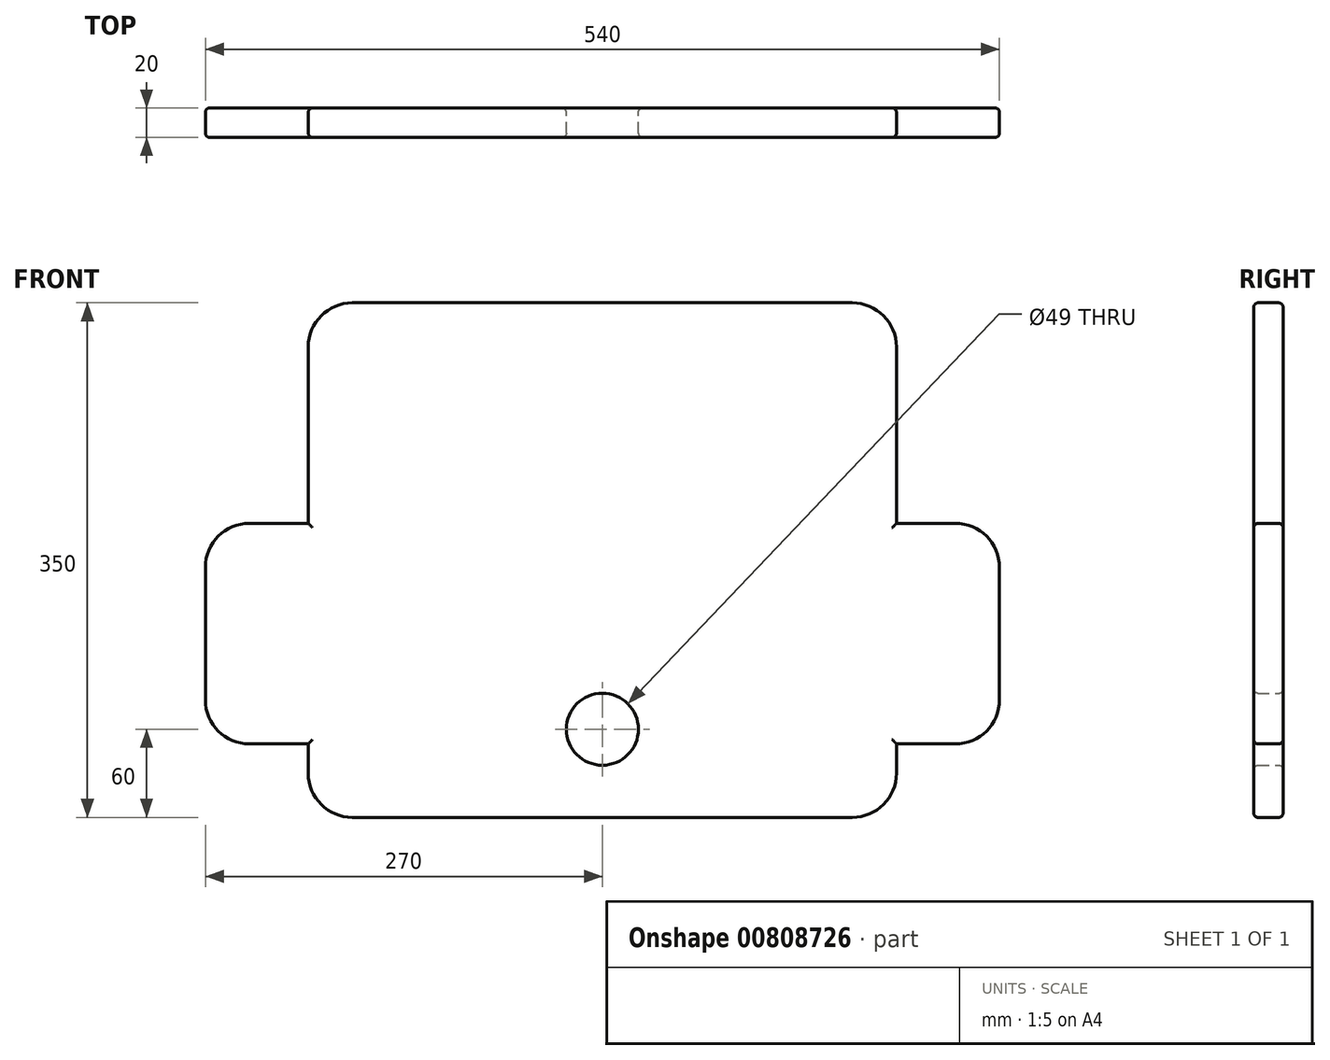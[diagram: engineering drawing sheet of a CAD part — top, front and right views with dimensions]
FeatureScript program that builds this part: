
annotation { "Feature Type Name" : "Feature", "Feature Type Description" : "" }
export const myFeature = defineFeature(function(context is Context, id is Id, definition is map)
    precondition{}
    {
        {
            var Q0;
            Q0=qCreatedBy(makeId("Front.planeOp"),FACE);
            var sketch = newSketch(context, id + "F0", { "sketchPlane" : qUnion([Q0])});
            skLineSegment(sketch, "E0.right", {"start": v(200, -135) * mm, "end": v(200, -115) * mm});
            skPoint(sketch, "E0.middle", {"position": v(0, 0) * mm});
            skLineSegment(sketch, "E1.bottom", {"start": v(200, -115) * mm, "end": v(240, -115) * mm});
            skLineSegment(sketch, "E1.top", {"start": v(200, 35) * mm, "end": v(240, 35) * mm});
            skLineSegment(sketch, "E1.right", {"start": v(270, -85) * mm, "end": v(270, 5) * mm});
            skLineSegment(sketch, "E2.trimOffspring", {"start": v(200, 35) * mm, "end": v(200, 155) * mm});
            skPoint(sketch, "E0.top.start.orphan", {"position": v(-200, 165) * mm});
            skPoint(sketch, "E0.bottom.start.orphan", {"position": v(-200, -185) * mm});
            skLineSegment(sketch, "E3", {"start": v(170, 185) * mm, "end": v(0, 185) * mm});
            skLineSegment(sketch, "E4", {"start": v(170, -165) * mm, "end": v(0, -165) * mm});
            skLineSegment(sketch, "E5.MirrorCS", {"start": v(-170, 185) * mm, "end": v(0, 185) * mm});
            skLineSegment(sketch, "E6.MirrorCS", {"start": v(-200, 35) * mm, "end": v(-200, 155) * mm});
            skLineSegment(sketch, "E7.MirrorCS", {"start": v(-200, 35) * mm, "end": v(-240, 35) * mm});
            skLineSegment(sketch, "E8.MirrorCS", {"start": v(-270, -85) * mm, "end": v(-270, 5) * mm});
            skLineSegment(sketch, "E9.MirrorCS", {"start": v(-200, -115) * mm, "end": v(-240, -115) * mm});
            skLineSegment(sketch, "E10.MirrorCS", {"start": v(-200, -135) * mm, "end": v(-200, -115) * mm});
            skLineSegment(sketch, "E11.MirrorCS", {"start": v(-170, -165) * mm, "end": v(0, -165) * mm});
            skPoint(sketch, "E12.visualSharp", {"position": v(200, 185) * mm});
            skArc(sketch, "E12.filletArc", {"start": v(200, 155) * mm, "mid": v(191.21, 176.21) * mm, "end": v(170, 185) * mm});
            skPoint(sketch, "E13.visualSharp", {"position": v(-200, 185) * mm});
            skArc(sketch, "E13.filletArc", {"start": v(-170, 185) * mm, "mid": v(-191.21, 176.21) * mm, "end": v(-200, 155) * mm});
            skPoint(sketch, "E14.visualSharp", {"position": v(-270, 35) * mm});
            skArc(sketch, "E14.filletArc", {"start": v(-240, 35) * mm, "mid": v(-261.21, 26.21) * mm, "end": v(-270, 5) * mm});
            skPoint(sketch, "E15.visualSharp", {"position": v(-270, -115) * mm});
            skArc(sketch, "E15.filletArc", {"start": v(-270, -85) * mm, "mid": v(-261.21, -106.21) * mm, "end": v(-240, -115) * mm});
            skPoint(sketch, "E16.visualSharp", {"position": v(-200, -165) * mm});
            skArc(sketch, "E16.filletArc", {"start": v(-200, -135) * mm, "mid": v(-191.21, -156.21) * mm, "end": v(-170, -165) * mm});
            skPoint(sketch, "E17.visualSharp", {"position": v(200, -165) * mm});
            skArc(sketch, "E17.filletArc", {"start": v(170, -165) * mm, "mid": v(191.21, -156.21) * mm, "end": v(200, -135) * mm});
            skPoint(sketch, "E18.visualSharp", {"position": v(270, -115) * mm});
            skArc(sketch, "E18.filletArc", {"start": v(240, -115) * mm, "mid": v(261.21, -106.21) * mm, "end": v(270, -85) * mm});
            skPoint(sketch, "E19.visualSharp", {"position": v(270, 35) * mm});
            skArc(sketch, "E19.filletArc", {"start": v(270, 5) * mm, "mid": v(261.21, 26.21) * mm, "end": v(240, 35) * mm});
            skLineSegment(sketch, "E20", {"start": v(0, -165) * mm, "end": v(0, -105) * mm, "construction": true});
            skCircle(sketch, "E21", {"center": v(0, -105) * mm, "radius": 24.5 * mm});
            skSolve(sketch);
        }
        {
            var Q0;
            Q0=makeQuery(id+"F0.imprint","IMPRINT",FACE,{"disambiguationData":[TD([[makeQuery(id+"F0.imprint","IMPRINT",EDGE,{"derivedFrom":sQuery(id+"F0.wireOp",EDGE,"E0.right")}),1.0]])]});
            extrude(context, id + "F1", {"entities" : qUnion([Q0]), "depth" : 20 * mm, "offsetDistance" : 25 * mm});
        }
        {
            var Q0;
            Q0=makeQuery(id+"F1.opExtrude","CAP_FACE",FACE,{"disambiguationData":[OSD([sQuery(id+"F0.wireOp",EDGE,"E0.right"),sQuery(id+"F0.wireOp",EDGE,"E1.bottom"),sQuery(id+"F0.wireOp",EDGE,"E1.top"),sQuery(id+"F0.wireOp",EDGE,"E1.right"),sQuery(id+"F0.wireOp",EDGE,"E2.trimOffspring"),sQuery(id+"F0.wireOp",EDGE,"E3"),sQuery(id+"F0.wireOp",EDGE,"E4"),sQuery(id+"F0.wireOp",EDGE,"E5.MirrorCS"),sQuery(id+"F0.wireOp",EDGE,"E6.MirrorCS"),sQuery(id+"F0.wireOp",EDGE,"E7.MirrorCS"),sQuery(id+"F0.wireOp",EDGE,"E8.MirrorCS"),sQuery(id+"F0.wireOp",EDGE,"E9.MirrorCS"),sQuery(id+"F0.wireOp",EDGE,"E10.MirrorCS"),sQuery(id+"F0.wireOp",EDGE,"E11.MirrorCS"),sQuery(id+"F0.wireOp",EDGE,"E12.filletArc"),sQuery(id+"F0.wireOp",EDGE,"E13.filletArc"),sQuery(id+"F0.wireOp",EDGE,"E14.filletArc"),sQuery(id+"F0.wireOp",EDGE,"E15.filletArc"),sQuery(id+"F0.wireOp",EDGE,"E16.filletArc"),sQuery(id+"F0.wireOp",EDGE,"E17.filletArc"),sQuery(id+"F0.wireOp",EDGE,"E18.filletArc"),sQuery(id+"F0.wireOp",EDGE,"E19.filletArc")])],"isStart":true});
            var Q1;
            Q1=makeQuery(id+"F1.opExtrude","CAP_FACE",FACE,{"disambiguationData":[OSD([sQuery(id+"F0.wireOp",EDGE,"E0.right"),sQuery(id+"F0.wireOp",EDGE,"E1.bottom"),sQuery(id+"F0.wireOp",EDGE,"E1.top"),sQuery(id+"F0.wireOp",EDGE,"E1.right"),sQuery(id+"F0.wireOp",EDGE,"E2.trimOffspring"),sQuery(id+"F0.wireOp",EDGE,"E3"),sQuery(id+"F0.wireOp",EDGE,"E4"),sQuery(id+"F0.wireOp",EDGE,"E5.MirrorCS"),sQuery(id+"F0.wireOp",EDGE,"E6.MirrorCS"),sQuery(id+"F0.wireOp",EDGE,"E7.MirrorCS"),sQuery(id+"F0.wireOp",EDGE,"E8.MirrorCS"),sQuery(id+"F0.wireOp",EDGE,"E9.MirrorCS"),sQuery(id+"F0.wireOp",EDGE,"E10.MirrorCS"),sQuery(id+"F0.wireOp",EDGE,"E11.MirrorCS"),sQuery(id+"F0.wireOp",EDGE,"E12.filletArc"),sQuery(id+"F0.wireOp",EDGE,"E13.filletArc"),sQuery(id+"F0.wireOp",EDGE,"E14.filletArc"),sQuery(id+"F0.wireOp",EDGE,"E15.filletArc"),sQuery(id+"F0.wireOp",EDGE,"E16.filletArc"),sQuery(id+"F0.wireOp",EDGE,"E17.filletArc"),sQuery(id+"F0.wireOp",EDGE,"E18.filletArc"),sQuery(id+"F0.wireOp",EDGE,"E19.filletArc")])],"isStart":false});
            fillet(context, id + "F2", {"entities" : qUnion([Q0, Q1]), "radius" : 3 * mm, "tangentPropagation" : true, "allowEdgeOverflow" : false});
        }
        {
            var Q0;
            Q0=makeQuery(id+"F1.opExtrude","CAP_FACE",FACE,{"disambiguationData":[OSD([sQuery(id+"F0.wireOp",EDGE,"E0.right"),sQuery(id+"F0.wireOp",EDGE,"E1.bottom"),sQuery(id+"F0.wireOp",EDGE,"E1.top"),sQuery(id+"F0.wireOp",EDGE,"E1.right"),sQuery(id+"F0.wireOp",EDGE,"E2.trimOffspring"),sQuery(id+"F0.wireOp",EDGE,"E3"),sQuery(id+"F0.wireOp",EDGE,"E4"),sQuery(id+"F0.wireOp",EDGE,"E5.MirrorCS"),sQuery(id+"F0.wireOp",EDGE,"E6.MirrorCS"),sQuery(id+"F0.wireOp",EDGE,"E7.MirrorCS"),sQuery(id+"F0.wireOp",EDGE,"E8.MirrorCS"),sQuery(id+"F0.wireOp",EDGE,"E9.MirrorCS"),sQuery(id+"F0.wireOp",EDGE,"E10.MirrorCS"),sQuery(id+"F0.wireOp",EDGE,"E11.MirrorCS"),sQuery(id+"F0.wireOp",EDGE,"E12.filletArc"),sQuery(id+"F0.wireOp",EDGE,"E13.filletArc"),sQuery(id+"F0.wireOp",EDGE,"E14.filletArc"),sQuery(id+"F0.wireOp",EDGE,"E15.filletArc"),sQuery(id+"F0.wireOp",EDGE,"E16.filletArc"),sQuery(id+"F0.wireOp",EDGE,"E17.filletArc"),sQuery(id+"F0.wireOp",EDGE,"E18.filletArc"),sQuery(id+"F0.wireOp",EDGE,"E19.filletArc")])],"isStart":true});
            var sketch = newSketch(context, id + "F3", { "sketchPlane" : qUnion([Q0])});
            skLineSegment(sketch, "E22.0", {"start": v(-200, -115) * mm, "end": v(-209, -115) * mm});
            skLineSegment(sketch, "E23", {"start": v(-209, -115) * mm, "end": v(-209, 35) * mm, "construction": true});
            skPoint(sketch, "E23.endSnap0", {"position": v(-220, 35) * mm});
            skPoint(sketch, "E24.trimOffspring.end.orphan", {"position": v(-200, 35) * mm});
            skPoint(sketch, "E25.0.start.orphan", {"position": v(-240, 35) * mm});
            skPoint(sketch, "E26.orphan", {"position": v(-240, -115) * mm});
            skPoint(sketch, "E27", {"position": v(-209, -40) * mm});
            skPoint(sketch, "E28.MirrorP", {"position": v(209, -40) * mm});
            skSolve(sketch);
        }
    });
